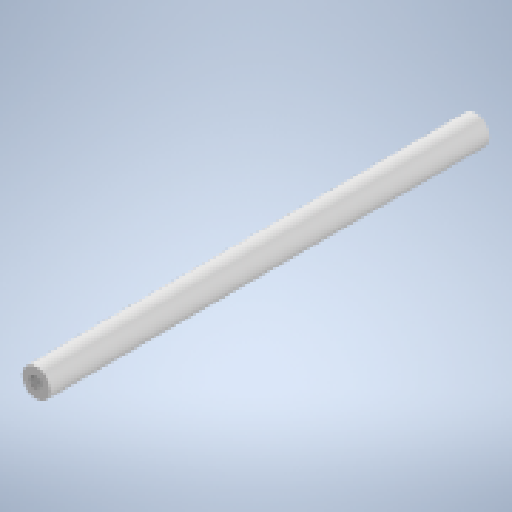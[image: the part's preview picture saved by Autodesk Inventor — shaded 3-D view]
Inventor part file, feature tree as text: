
AUTODESK INVENTOR PART (.ipt)
format: ipt  version: 2023 (Build 270158000, 158)  size: 151,552 bytes
history: native  units: mm
features: extrude x3, sketch x3, thread x2
ambient origin geometry x8: Origin, YZ Plane, XZ Plane, XY Plane, X Axis, Y Axis, Z Axis, Center Point
bodies: Solid1 (feature_tree)
feature tree (8):
  extrude  "Extrusion1"  Depth=75.0mm TaperAngle=0.0deg
  extrude  "Extrusion2"  Depth=20.0mm TaperAngle=0.0deg
  extrude  "Extrusion3"  Depth=20.0mm TaperAngle=0.0deg
  thread  "Thread1"  [1 undecoded]
  thread  "Thread2"  [1 undecoded]
  sketch  "Sketch1"  dims[d0=5.0mm d1=75.0mm d2=0.0mm]
  sketch  "Sketch2"  dims[d3=2.2mm d4=20.0mm d5=0.0mm]
  sketch  "Sketch3"  dims[d6=20.0mm d7=0.0mm d8=16.0mm d9=0.0mm d10=16.0mm d11=0.0mm]
note: 2 required parameter values undecoded (feature->parameter linkage not recoverable at this tier; creation-order binding heuristic only, values carry confidence <= 0.55)
